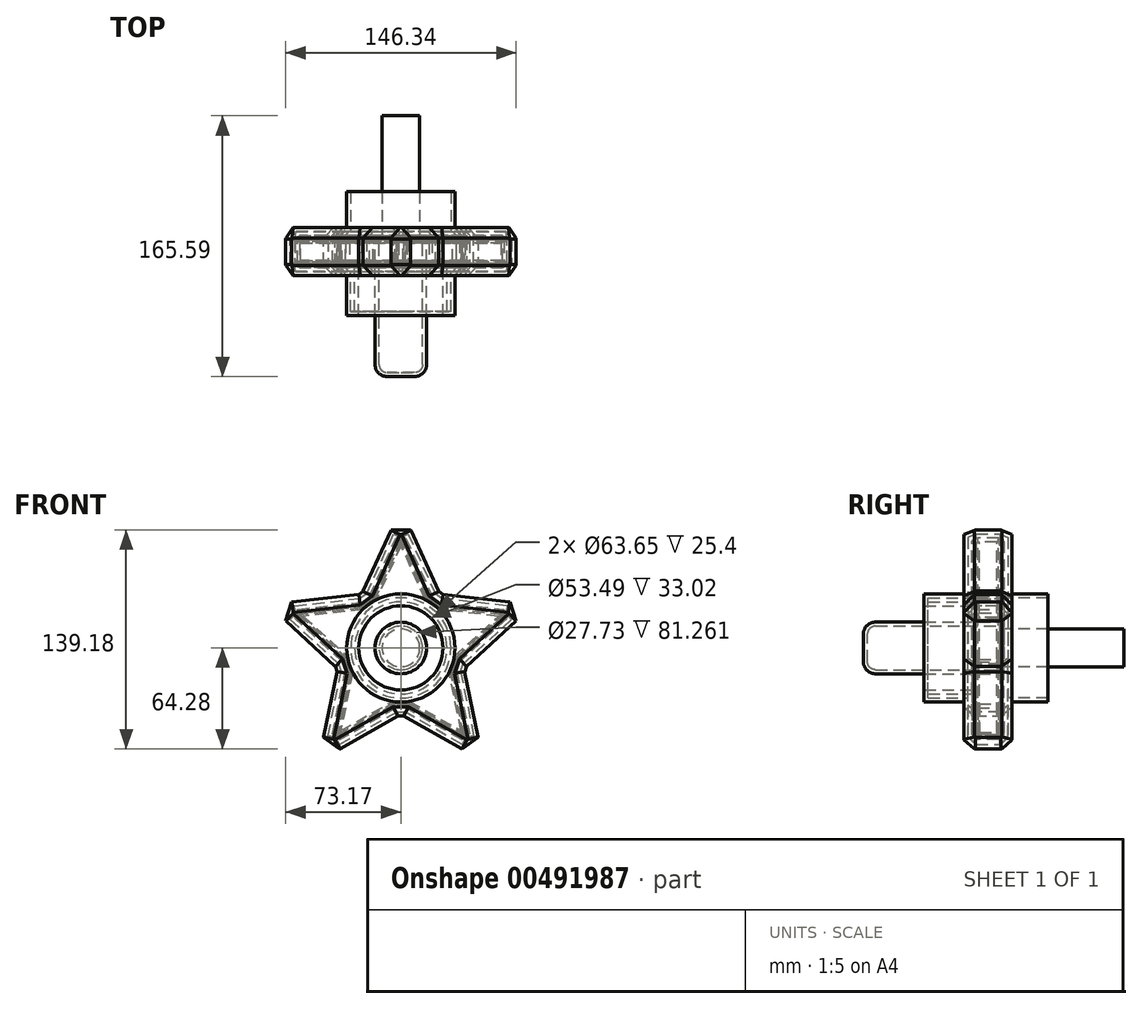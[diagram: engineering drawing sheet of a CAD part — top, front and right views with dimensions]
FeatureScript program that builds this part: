
annotation { "Feature Type Name" : "Feature", "Feature Type Description" : "" }
export const myFeature = defineFeature(function(context is Context, id is Id, definition is map)
    precondition{}
    {
        {
            var Q0;
            Q0=qCreatedBy(makeId("Front.planeOp"),FACE);
            var sketch = newSketch(context, id + "F0", { "sketchPlane" : qUnion([Q0])});
            skCircle(sketch, "E0", {"center": v(0, 0) * mm, "radius": 31.75 * mm});
            skCircle(sketch, "E1.cCircle", {"center": v(0, 0) * mm, "radius": 31.75 * mm, "construction": true});
            skLineSegment(sketch, "E1.0", {"start": v(23.07, 31.75) * mm, "end": v(37.32, -12.13) * mm});
            skLineSegment(sketch, "E1.1", {"start": v(37.32, -12.13) * mm, "end": v(0, -39.25) * mm});
            skLineSegment(sketch, "E1.2", {"start": v(0, -39.25) * mm, "end": v(-37.32, -12.13) * mm});
            skLineSegment(sketch, "E1.3", {"start": v(-37.32, -12.13) * mm, "end": v(-23.07, 31.75) * mm});
            skLineSegment(sketch, "E1.4", {"start": v(-23.07, 31.75) * mm, "end": v(23.07, 31.75) * mm});
            skPoint(sketch, "E1.0.midPoint", {"position": v(30.2, 9.81) * mm});
            skLineSegment(sketch, "E2", {"start": v(-37.32, -12.13) * mm, "end": v(-48.52, -66.78) * mm});
            skLineSegment(sketch, "E3", {"start": v(-48.52, -66.78) * mm, "end": v(0, -39.25) * mm});
            skLineSegment(sketch, "E4", {"start": v(0, -39.25) * mm, "end": v(48.52, -66.78) * mm});
            skLineSegment(sketch, "E5", {"start": v(48.52, -66.78) * mm, "end": v(37.32, -12.13) * mm});
            skLineSegment(sketch, "E6", {"start": v(37.32, -12.13) * mm, "end": v(78.5, 25.5) * mm});
            skLineSegment(sketch, "E7", {"start": v(78.5, 25.5) * mm, "end": v(23.07, 31.75) * mm});
            skLineSegment(sketch, "E8", {"start": v(23.07, 31.75) * mm, "end": v(0, 82.55) * mm});
            skLineSegment(sketch, "E9", {"start": v(0, 82.55) * mm, "end": v(-23.07, 31.75) * mm});
            skLineSegment(sketch, "E10", {"start": v(-23.07, 31.75) * mm, "end": v(-78.5, 25.5) * mm});
            skLineSegment(sketch, "E11", {"start": v(-78.5, 25.5) * mm, "end": v(-37.32, -12.13) * mm});
            skSolve(sketch);
        }
        {
            var Q0;
            {var subQ3=sQuery(id+"F0.wireOp",EDGE,"E8");Q0=makeQuery(id+"F0.imprint","IMPRINT",FACE,{"disambiguationData":[TD([[makeQuery(id+"F0.imprint","IMPRINT",EDGE,{"derivedFrom":subQ3}),1.0]])]});}
            var Q1;
            {var subQ3=sQuery(id+"F0.wireOp",EDGE,"E6");Q1=makeQuery(id+"F0.imprint","IMPRINT",FACE,{"disambiguationData":[TD([[makeQuery(id+"F0.imprint","IMPRINT",EDGE,{"derivedFrom":subQ3}),1.0]])]});}
            var Q2;
            {var subQ0=sQuery(id+"F0.wireOp",EDGE,"E1.4");var subQ1=sQuery(id+"F0.wireOp",EDGE,"E0");var subQ2=makeQuery(id+"F0.imprint","INTERSECT",VERTEX,{"derivedFrom":[subQ1,subQ0]});Q2=makeQuery(id+"F0.imprint","IMPRINT",FACE,{"disambiguationData":[TD([[makeQuery(id+"F0.imprint","IMPRINT",EDGE,{"disambiguationData":[TD([[subQ2,-1.0]])],"derivedFrom":subQ1}),-1.0]])]});}
            var Q3;
            {var subQ0=sQuery(id+"F0.wireOp",EDGE,"E1.4");var subQ1=sQuery(id+"F0.wireOp",EDGE,"E0");var subQ2=makeQuery(id+"F0.imprint","INTERSECT",VERTEX,{"derivedFrom":[subQ1,subQ0]});Q3=makeQuery(id+"F0.imprint","IMPRINT",FACE,{"disambiguationData":[TD([[makeQuery(id+"F0.imprint","IMPRINT",EDGE,{"disambiguationData":[TD([[subQ2,1.0]])],"derivedFrom":subQ1}),-1.0]])]});}
            var Q4;
            {var subQ0=sQuery(id+"F0.wireOp",EDGE,"E1.3");var subQ1=sQuery(id+"F0.wireOp",EDGE,"E0");var subQ2=makeQuery(id+"F0.imprint","INTERSECT",VERTEX,{"derivedFrom":[subQ1,subQ0]});Q4=makeQuery(id+"F0.imprint","IMPRINT",FACE,{"disambiguationData":[TD([[makeQuery(id+"F0.imprint","IMPRINT",EDGE,{"disambiguationData":[TD([[subQ2,-1.0]])],"derivedFrom":subQ1}),-1.0]])]});}
            var Q5;
            {var subQ0=sQuery(id+"F0.wireOp",EDGE,"E1.2");var subQ1=sQuery(id+"F0.wireOp",EDGE,"E0");var subQ2=makeQuery(id+"F0.imprint","INTERSECT",VERTEX,{"derivedFrom":[subQ1,subQ0]});Q5=makeQuery(id+"F0.imprint","IMPRINT",FACE,{"disambiguationData":[TD([[makeQuery(id+"F0.imprint","IMPRINT",EDGE,{"disambiguationData":[TD([[subQ2,-1.0]])],"derivedFrom":subQ1}),-1.0]])]});}
            var Q6;
            {var subQ0=sQuery(id+"F0.wireOp",EDGE,"E1.0");var subQ1=sQuery(id+"F0.wireOp",EDGE,"E0");var subQ2=makeQuery(id+"F0.imprint","INTERSECT",VERTEX,{"derivedFrom":[subQ1,subQ0]});Q6=makeQuery(id+"F0.imprint","IMPRINT",FACE,{"disambiguationData":[TD([[makeQuery(id+"F0.imprint","IMPRINT",EDGE,{"disambiguationData":[TD([[subQ2,1.0]])],"derivedFrom":subQ1}),-1.0]])]});}
            var Q7;
            {var subQ3=sQuery(id+"F0.wireOp",EDGE,"E4");Q7=makeQuery(id+"F0.imprint","IMPRINT",FACE,{"disambiguationData":[TD([[makeQuery(id+"F0.imprint","IMPRINT",EDGE,{"derivedFrom":subQ3}),1.0]])]});}
            var Q8;
            {var subQ3=sQuery(id+"F0.wireOp",EDGE,"E2");Q8=makeQuery(id+"F0.imprint","IMPRINT",FACE,{"disambiguationData":[TD([[makeQuery(id+"F0.imprint","IMPRINT",EDGE,{"derivedFrom":subQ3}),1.0]])]});}
            var Q9;
            {var subQ3=sQuery(id+"F0.wireOp",EDGE,"E10");Q9=makeQuery(id+"F0.imprint","IMPRINT",FACE,{"disambiguationData":[TD([[makeQuery(id+"F0.imprint","IMPRINT",EDGE,{"derivedFrom":subQ3}),1.0]])]});}
            var Q10;
            {var subQ0=sQuery(id+"F0.wireOp",EDGE,"E0");var subQ4=makeQuery(id+"F0.imprint","INTERSECT",VERTEX,{"derivedFrom":[subQ0,sQuery(id+"F0.wireOp",EDGE,"E1.4")]});Q10=makeQuery(id+"F0.imprint","IMPRINT",FACE,{"disambiguationData":[TD([[makeQuery(id+"F0.imprint","IMPRINT",EDGE,{"disambiguationData":[TD([[subQ4,1.0]])],"derivedFrom":subQ0}),1.0]])]});}
            extrude(context, id + "F1", {"entities" : qUnion([Q0, Q1, Q2, Q3, Q4, Q5, Q6, Q7, Q8, Q9, Q10]), "endBound" : BoundingType.SYMMETRIC, "depth" : 25.4 * mm});
        }
        {
            var Q0;
            Q0=makeQuery(id+"F1.opExtrude","SWEPT_EDGE",EDGE,{"disambiguationData":[OSD([sQuery(id+"F0.wireOp",EDGE,"E8"),sQuery(id+"F0.wireOp",EDGE,"E9")])]});
            var Q1;
            Q1=makeQuery(id+"F1.opExtrude","SWEPT_EDGE",EDGE,{"disambiguationData":[OSD([sQuery(id+"F0.wireOp",EDGE,"E6"),sQuery(id+"F0.wireOp",EDGE,"E7")])]});
            var Q2;
            Q2=makeQuery(id+"F1.opExtrude","SWEPT_EDGE",EDGE,{"disambiguationData":[OSD([sQuery(id+"F0.wireOp",EDGE,"E4"),sQuery(id+"F0.wireOp",EDGE,"E5")])]});
            var Q3;
            Q3=makeQuery(id+"F1.opExtrude","SWEPT_EDGE",EDGE,{"disambiguationData":[OSD([sQuery(id+"F0.wireOp",EDGE,"E2"),sQuery(id+"F0.wireOp",EDGE,"E3")])]});
            var Q4;
            Q4=makeQuery(id+"F1.opExtrude","SWEPT_EDGE",EDGE,{"disambiguationData":[OSD([sQuery(id+"F0.wireOp",EDGE,"E1.2"),sQuery(id+"F0.wireOp",EDGE,"E1.3"),sQuery(id+"F0.wireOp",EDGE,"E2"),sQuery(id+"F0.wireOp",EDGE,"E11")])]});
            var Q5;
            Q5=makeQuery(id+"F1.opExtrude","SWEPT_EDGE",EDGE,{"disambiguationData":[OSD([sQuery(id+"F0.wireOp",EDGE,"E1.3"),sQuery(id+"F0.wireOp",EDGE,"E1.4"),sQuery(id+"F0.wireOp",EDGE,"E9"),sQuery(id+"F0.wireOp",EDGE,"E10")])]});
            var Q6;
            Q6=makeQuery(id+"F1.opExtrude","SWEPT_EDGE",EDGE,{"disambiguationData":[OSD([sQuery(id+"F0.wireOp",EDGE,"E1.0"),sQuery(id+"F0.wireOp",EDGE,"E1.4"),sQuery(id+"F0.wireOp",EDGE,"E7"),sQuery(id+"F0.wireOp",EDGE,"E8")])]});
            var Q7;
            Q7=makeQuery(id+"F1.opExtrude","SWEPT_FACE",FACE,{"disambiguationData":[OSD([sQuery(id+"F0.wireOp",EDGE,"E5")])]});
            var Q8;
            Q8=makeQuery(id+"F1.opExtrude","SWEPT_FACE",FACE,{"disambiguationData":[OSD([sQuery(id+"F0.wireOp",EDGE,"E4")])]});
            var Q9;
            Q9=makeQuery(id+"F1.opExtrude","SWEPT_FACE",FACE,{"disambiguationData":[OSD([sQuery(id+"F0.wireOp",EDGE,"E8")])]});
            var Q10;
            Q10=makeQuery(id+"F1.opExtrude","SWEPT_FACE",FACE,{"disambiguationData":[OSD([sQuery(id+"F0.wireOp",EDGE,"E10")])]});
            var Q11;
            Q11=makeQuery(id+"F1.opExtrude","SWEPT_FACE",FACE,{"disambiguationData":[OSD([sQuery(id+"F0.wireOp",EDGE,"E2")])]});
            chamfer(context, id + "F2", {"entities" : qUnion([Q0, Q1, Q2, Q3, Q4, Q5, Q6, Q7, Q8, Q9, Q10, Q11]), "width" : 5.08 * mm, "tangentPropagation" : true});
        }
        {
            var Q0;
            Q0=makeQuery(id+"F1.opExtrude","CAP_FACE",FACE,{"disambiguationData":[OSD([sQuery(id+"F0.wireOp",EDGE,"E2"),sQuery(id+"F0.wireOp",EDGE,"E3"),sQuery(id+"F0.wireOp",EDGE,"E4"),sQuery(id+"F0.wireOp",EDGE,"E5"),sQuery(id+"F0.wireOp",EDGE,"E6"),sQuery(id+"F0.wireOp",EDGE,"E7"),sQuery(id+"F0.wireOp",EDGE,"E8"),sQuery(id+"F0.wireOp",EDGE,"E9"),sQuery(id+"F0.wireOp",EDGE,"E10"),sQuery(id+"F0.wireOp",EDGE,"E11")])],"isStart":false});
            var sketch = newSketch(context, id + "F3", { "sketchPlane" : qUnion([Q0])});
            skCircle(sketch, "E12", {"center": v(0, 0) * mm, "radius": 31.82 * mm});
            skSolve(sketch);
        }
        {
            var Q0;
            Q0=makeQuery(id+"F3.imprint","IMPRINT",FACE,{"disambiguationData":[TD([[makeQuery(id+"F3.imprint","IMPRINT",EDGE,{"derivedFrom":sQuery(id+"F3.wireOp",EDGE,"E12")}),1.0]])]});
            extrude(context, id + "F4", {"entities" : qUnion([Q0]), "operationType" : NewBodyOperationType.ADD, "depth" : 25.4 * mm});
        }
        {
            var Q0;
            Q0=makeQuery(id+"F4.opExtrude","CAP_FACE",FACE,{"disambiguationData":[OSD([sQuery(id+"F3.wireOp",EDGE,"E12")])],"isStart":false});
            var Q1;
            Q1=makeQuery(id+"F1.opExtrude","SWEPT_BODY",BODY,{"disambiguationData":[OSD([sQuery(id+"F0.wireOp",EDGE,"E2"),sQuery(id+"F0.wireOp",EDGE,"E3"),sQuery(id+"F0.wireOp",EDGE,"E4"),sQuery(id+"F0.wireOp",EDGE,"E5"),sQuery(id+"F0.wireOp",EDGE,"E6"),sQuery(id+"F0.wireOp",EDGE,"E7"),sQuery(id+"F0.wireOp",EDGE,"E8"),sQuery(id+"F0.wireOp",EDGE,"E9"),sQuery(id+"F0.wireOp",EDGE,"E10"),sQuery(id+"F0.wireOp",EDGE,"E11")])]});
            shell(context, id + "F5", {"entities" : qUnion([Q0]), "parts" : qUnion([Q1]), "thickness" : 2.54 * mm});
        }
        {
            var Q0;
            {var subQ0=sQuery(id+"F0.wireOp",EDGE,"E11");var subQ1=sQuery(id+"F0.wireOp",EDGE,"E10");var subQ2=sQuery(id+"F0.wireOp",EDGE,"E9");var subQ3=sQuery(id+"F0.wireOp",EDGE,"E8");var subQ4=sQuery(id+"F0.wireOp",EDGE,"E7");var subQ5=sQuery(id+"F0.wireOp",EDGE,"E6");var subQ6=sQuery(id+"F0.wireOp",EDGE,"E5");var subQ7=sQuery(id+"F0.wireOp",EDGE,"E4");var subQ8=sQuery(id+"F0.wireOp",EDGE,"E3");var subQ9=sQuery(id+"F0.wireOp",EDGE,"E2");Q0=makeQuery(id+"F5.opShell","OFFSET_FACE",FACE,{"disambiguationData":[OSD([subQ9,subQ8,subQ7,subQ6,subQ5,subQ4,subQ3,subQ2,subQ1,subQ0]),TDD([makeQuery(id+"F1.opExtrude","CAP_FACE",FACE,{"disambiguationData":[OSD([subQ9,subQ8,subQ7,subQ6,subQ5,subQ4,subQ3,subQ2,subQ1,subQ0])],"isStart":true})])]});}
            var sketch = newSketch(context, id + "F6", { "sketchPlane" : qUnion([Q0])});
            skCircle(sketch, "E13", {"center": v(0, 0) * mm, "radius": 13.86 * mm});
            skSolve(sketch);
        }
        {
            var Q0;
            Q0=makeQuery(id+"F6.imprint","IMPRINT",FACE,{"disambiguationData":[TD([[makeQuery(id+"F6.imprint","IMPRINT",EDGE,{"derivedFrom":sQuery(id+"F6.wireOp",EDGE,"E13")}),1.0]])]});
            extrude(context, id + "F7", {"entities" : qUnion([Q0]), "operationType" : NewBodyOperationType.ADD, "depth" : 86.85 * mm});
        }
        {
            var Q0;
            Q0=makeQuery(id+"F7.opExtrude","CAP_FACE",FACE,{"disambiguationData":[OSD([sQuery(id+"F6.wireOp",EDGE,"E13")])],"isStart":false});
            fillet(context, id + "F8", {"entities" : qUnion([Q0]), "radius" : 5.08 * mm, "tangentPropagation" : true, "allowEdgeOverflow" : false});
        }
        {
            var Q0;
            Q0=makeQuery(id+"F1.opExtrude","CAP_FACE",FACE,{"disambiguationData":[OSD([sQuery(id+"F0.wireOp",EDGE,"E2"),sQuery(id+"F0.wireOp",EDGE,"E3"),sQuery(id+"F0.wireOp",EDGE,"E4"),sQuery(id+"F0.wireOp",EDGE,"E5"),sQuery(id+"F0.wireOp",EDGE,"E6"),sQuery(id+"F0.wireOp",EDGE,"E7"),sQuery(id+"F0.wireOp",EDGE,"E8"),sQuery(id+"F0.wireOp",EDGE,"E9"),sQuery(id+"F0.wireOp",EDGE,"E10"),sQuery(id+"F0.wireOp",EDGE,"E11")])],"isStart":true});
            var sketch = newSketch(context, id + "F9", { "sketchPlane" : qUnion([Q0])});
            skCircle(sketch, "E14", {"center": v(0, 0) * mm, "radius": 31.82 * mm});
            skSolve(sketch);
        }
        {
            var Q0;
            Q0 = qSketchRegion(id + "F9", true);
            extrude(context, id + "F10", {"entities" : qUnion([Q0]), "operationType" : NewBodyOperationType.ADD, "depth" : 25.4 * mm});
        }
        {
            var Q0;
            Q0=makeQuery(id+"F10.opExtrude","CAP_FACE",FACE,{"disambiguationData":[OSD([sQuery(id+"F9.wireOp",EDGE,"E14")])],"isStart":false});
            shell(context, id + "F11", {"entities" : qUnion([Q0]), "thickness" : 2.54 * mm, "oppositeDirection" : true});
        }
        {
            var Q0;
            {var subQ0=sQuery(id+"F0.wireOp",EDGE,"E11");var subQ1=sQuery(id+"F0.wireOp",EDGE,"E10");var subQ2=sQuery(id+"F0.wireOp",EDGE,"E9");var subQ3=sQuery(id+"F0.wireOp",EDGE,"E8");var subQ4=sQuery(id+"F0.wireOp",EDGE,"E7");var subQ5=sQuery(id+"F0.wireOp",EDGE,"E6");var subQ6=sQuery(id+"F0.wireOp",EDGE,"E5");var subQ7=sQuery(id+"F0.wireOp",EDGE,"E4");var subQ8=sQuery(id+"F0.wireOp",EDGE,"E3");var subQ9=sQuery(id+"F0.wireOp",EDGE,"E2");Q0=makeQuery(id+"F11.opShell","OFFSET_FACE",FACE,{"disambiguationData":[OSD([subQ9,subQ8,subQ7,subQ6,subQ5,subQ4,subQ3,subQ2,subQ1,subQ0]),TDD([makeQuery(id+"F5.opShell","OFFSET_FACE",FACE,{"disambiguationData":[OSD([subQ9,subQ8,subQ7,subQ6,subQ5,subQ4,subQ3,subQ2,subQ1,subQ0]),TDD([makeQuery(id+"F1.opExtrude","CAP_FACE",FACE,{"disambiguationData":[OSD([subQ9,subQ8,subQ7,subQ6,subQ5,subQ4,subQ3,subQ2,subQ1,subQ0])],"isStart":true})])]})])]});}
            var sketch = newSketch(context, id + "F12", { "sketchPlane" : qUnion([Q0])});
            skLineSegment(sketch, "E15.bottom", {"start": v(-17.43, 18.97) * mm, "end": v(19.61, 18.97) * mm});
            skLineSegment(sketch, "E15.top", {"start": v(-17.43, -17.58) * mm, "end": v(19.61, -17.58) * mm});
            skLineSegment(sketch, "E15.left", {"start": v(-17.43, 18.97) * mm, "end": v(-17.43, -17.58) * mm});
            skLineSegment(sketch, "E15.right", {"start": v(19.61, 18.97) * mm, "end": v(19.61, -17.58) * mm});
            skSolve(sketch);
        }
        {
            var Q0;
            Q0 = qSketchRegion(id + "F12", true);
            extrude(context, id + "F13", {"entities" : qUnion([Q0]), "operationType" : NewBodyOperationType.ADD, "oppositeDirection" : true, "depth" : 0.5 * mm});
        }
        {
            var Q0;
            {var subQ0=sQuery(id+"F0.wireOp",EDGE,"E11");var subQ1=sQuery(id+"F0.wireOp",EDGE,"E10");var subQ2=sQuery(id+"F0.wireOp",EDGE,"E9");var subQ3=sQuery(id+"F0.wireOp",EDGE,"E8");var subQ4=sQuery(id+"F0.wireOp",EDGE,"E7");var subQ5=sQuery(id+"F0.wireOp",EDGE,"E6");var subQ6=sQuery(id+"F0.wireOp",EDGE,"E5");var subQ7=sQuery(id+"F0.wireOp",EDGE,"E4");var subQ8=sQuery(id+"F0.wireOp",EDGE,"E3");var subQ9=sQuery(id+"F0.wireOp",EDGE,"E2");Q0=makeQuery(id+"F13.boolean.opBoolean","MERGE",FACE,{"derivedFrom":[makeQuery(id+"F11.opShell","OFFSET_FACE",FACE,{"disambiguationData":[OSD([subQ9,subQ8,subQ7,subQ6,subQ5,subQ4,subQ3,subQ2,subQ1,subQ0]),TDD([makeQuery(id+"F5.opShell","OFFSET_FACE",FACE,{"disambiguationData":[OSD([subQ9,subQ8,subQ7,subQ6,subQ5,subQ4,subQ3,subQ2,subQ1,subQ0]),TDD([makeQuery(id+"F1.opExtrude","CAP_FACE",FACE,{"disambiguationData":[OSD([subQ9,subQ8,subQ7,subQ6,subQ5,subQ4,subQ3,subQ2,subQ1,subQ0])],"isStart":true})])]})])]}),makeQuery(id+"F13.opExtrude","CAP_FACE",FACE,{"disambiguationData":[OSD([sQuery(id+"F12.wireOp",EDGE,"E15.bottom"),sQuery(id+"F12.wireOp",EDGE,"E15.top"),sQuery(id+"F12.wireOp",EDGE,"E15.left"),sQuery(id+"F12.wireOp",EDGE,"E15.right")])],"isStart":true})]});}
            var sketch = newSketch(context, id + "F14", { "sketchPlane" : qUnion([Q0])});
            skCircle(sketch, "E16", {"center": v(0, 0) * mm, "radius": 11.97 * mm});
            skSolve(sketch);
        }
        {
            var Q0;
            Q0 = qSketchRegion(id + "F14", true);
            extrude(context, id + "F15", {"entities" : qUnion([Q0]), "operationType" : NewBodyOperationType.ADD, "depth" : 76.2 * mm});
        }
    });
